# Revit family: sh-13107
name_source: partatom
category: Lighting Fixtures
revit_build: Autodesk Revit 2017 (Build: 20160225_1515(x64)
units: mm (PartAtom-declared; Revit-internal decimal feet)

## family parameters
Always vertical = Yes
Cut with Voids When Loaded = No
Host = Wall
Light Source = No
OmniClass Number = 23.80.70.00
OmniClass Title = Lighting
Part Type = Normal
Room Calculation Point = No
Round Connector Dimension = Use Diameter
Shared = Yes

## types (2) — shared parameters
Body Material = Aluminum
Cost = 1 $
Flicker = Free Flicker
Height = 17.5 cm
IP = 65
Lamp = LED
Manufacturer = SHOA
Model = SH-13107
Protection Class = class I
Type medule = COB
URL = https://www.shoaco.com
Voltage/Frequency = 230 V Ac/50HZ
Website = www.shoaco.com
Width = 10.6 cm
color rendering index(CRI) = 80
color temperature = 3000K
consumption current = 0 A
instalation = Wall Mounted
wattage. = 12 W

## per-type parameters (varying)
| type | Body color |
| SH-13107(Gray body-3000K-LED) | Gray |
| SH-13107(white body-3000K-LED) | White |

## geometry (parser evidence)
native form markers: Sweep x4
no freeform markers — native parametric forms only
